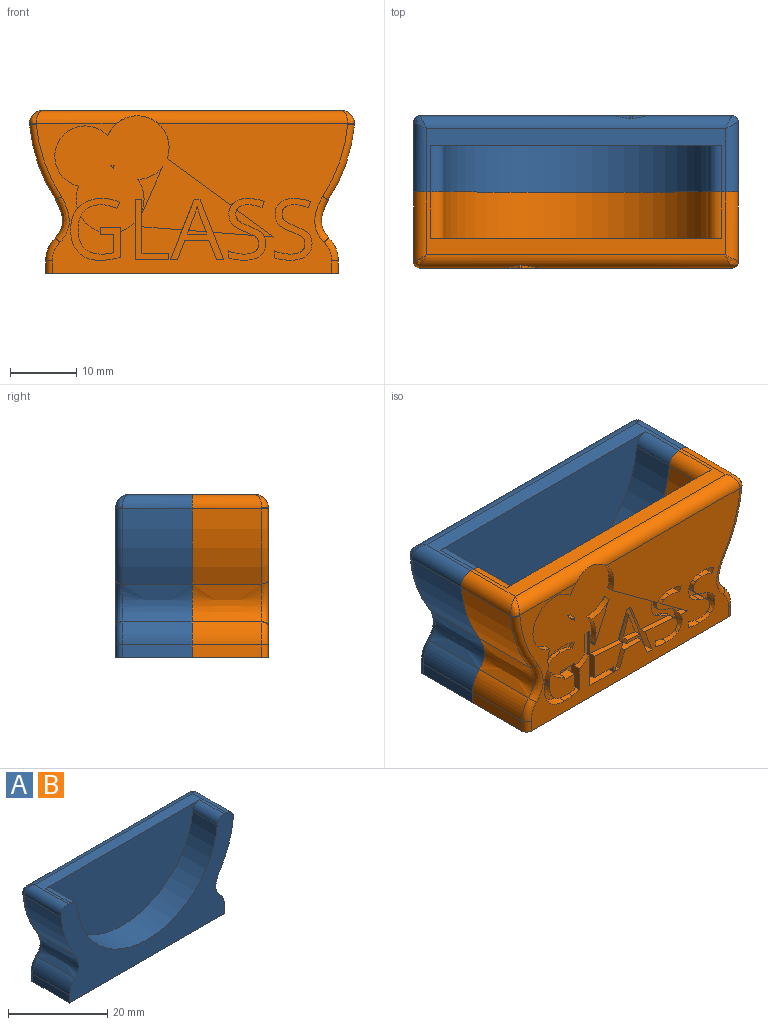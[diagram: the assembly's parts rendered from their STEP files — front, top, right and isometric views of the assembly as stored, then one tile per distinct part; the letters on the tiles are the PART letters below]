
ASSEMBLY  parts=2 mates=1
PART A: 149 faces, bbox 53x11.5x24.6 mm
  f0: plane 46.98x22.58mm, normal (0,1,0), area 539.3mm2, adj f3,f5,f8,f9,f10,f11,f12,f22
  f1: plane 5.75x5.37mm, normal (0,1,0), area 18.2mm2, adj f4,f84,f85,f88,f89,f90,f91,f92
  f2: plane 7.04x3.75mm, normal (0,1,0), area 6.8mm2, adj f6,f7,f27,f77
  f3: cylinder r=5.13mm len=2.17mm, axis (0,1,0), area 2.6mm2, adj f0,f13,f76,f83
  f4: cylinder r=5.13mm len=2.94mm, axis (0,1,0), area 3.8mm2, adj f1,f13,f84,f85
  f5: cylinder r=5.13mm len=3.39mm, axis (0,1,0), area 3.5mm2, adj f0,f13,f26,f86
  f6: cylinder r=5.13mm len=4.74mm, axis (0,1,0), area 5mm2, adj f2,f13,f27,f77
  f7: plane 7.04x3.12mm, normal (-0.91,0,-0.4), area 7.7mm2, adj f2,f13,f27,f77
  f8: plane 6.04x1mm, normal (-0.08,0,1), area 6.1mm2, adj f0,f13,f59,f77
  f9: plane 6.11x1mm, normal (-0.08,0,1), area 6.1mm2, adj f0,f13,f33,f60
  f10: plane 1.44x1mm, normal (-0.08,0,1), area 1.4mm2, adj f0,f11,f14,f34
  f11: plane 5.59x4.1mm, normal (0.59,0,-0.81), area 6.9mm2, adj f0,f10,f14,f35
  f12: plane 9.65x7.08mm, normal (0.59,0,-0.81), area 12mm2, adj f0,f13,f31,f36
  f13: plane 29.97x18.05mm, normal (0,1,0), area 275.3mm2, adj f3,f4,f5,f6,f7,f8,f9,f12
  f14: plane 5.72x4.11mm, normal (0,1,0), area 5.1mm2, adj f10,f11,f34,f35,f46,f47,f48,f49
  f15: extruded ~10.5x5.69mm, area 65mm2, adj f16,f24,f141,f145
  f16: cylinder r=24.58mm len=11.32mm, axis (0,1,0), area 127.1mm2, adj f15,f24,f131,f142
  f17: cylinder r=20mm len=39.83mm, axis (0,1,0), area 414.3mm2, adj f24,f25,f133,f134
  f18: plane 44.98x9.5mm, normal (0,0,1), area 120.6mm2, adj f24,f25,f130,f131,f132,f133,f134
  f19: cylinder r=24.58mm len=11.32mm, axis (0,1,0), area 127.1mm2, adj f20,f24,f130,f137
  f20: extruded ~10.5x5.69mm, area 65mm2, adj f19,f24,f136,f147
  f21: plane 10.5x1.89mm, normal (-1,0,0), area 19.9mm2, adj f22,f24,f135,f147
  f22: plane 44.12x11.5mm, normal (0,0,-1), area 506.9mm2, adj f0,f21,f23,f24,f135,f140
  f23: plane 10.5x1.89mm, normal (1,0,0), area 19.9mm2, adj f22,f24,f140,f145
  f24: plane 48.98x24.58mm, normal (0,-1,0), area 457.7mm2, adj f15,f16,f17,f18,f19,f20,f21,f22
  f25: plane 43.82x20mm, normal (0,-1,0), area 629.8mm2, adj f17,f18,f133,f134
  f26: cylinder r=4.59mm len=9.07mm, axis (0,1,0), area 17.2mm2, adj f0,f5,f13,f31
  f27: cylinder r=4.8mm len=3.75mm, axis (0,1,0), area 4.3mm2, adj f2,f6,f7,f13
  f28: cylinder r=4.59mm len=1mm, axis (0,1,0), area 0.5mm2, adj f13,f29,f30,f32
  f29: cylinder r=4.8mm len=1mm, axis (0,1,0), area 0.6mm2, adj f13,f28,f30,f32
  f30: cylinder r=5.13mm len=1mm, axis (0,1,0), area 0.6mm2, adj f13,f28,f29,f32
  f31: cylinder r=4.8mm len=9.26mm, axis (0,1,0), area 15mm2, adj f0,f12,f13,f26,f132
  f32: plane 0.55x0.5mm, normal (0,1,0), area 0.1mm2, adj f28,f29,f30
  f33: extruded ~1.6x0.63mm, area 1.3mm2, adj f0,f9,f13,f37,f57,f58
  f34: extruded ~1.6x1.51mm, area 2.1mm2, adj f0,f10,f14,f45,f46,f58
  f35: extruded ~1.6x1mm, area 1.2mm2, adj f0,f11,f14,f49,f50,f58
  f36: extruded ~1.67x1.6mm, area 1.8mm2, adj f0,f12,f13,f54,f55,f58
  f37: extruded ~1.6x0.77mm, area 1.3mm2, adj f0,f33,f38,f58
  f38: extruded ~1.6x1.11mm, area 2.1mm2, adj f0,f37,f39,f58
  f39: extruded ~1.6x1.59mm, area 2.7mm2, adj f0,f38,f40,f58
  f40: extruded ~1.6x1.3mm, area 2.1mm2, adj f0,f39,f41,f58
  f41: extruded ~1.6x1.22mm, area 2mm2, adj f0,f40,f42,f58
  f42: plane 1.6x1.02mm, normal (-1,0,0), area 1.6mm2, adj f0,f41,f43,f58
  f43: extruded ~2.48x1.6mm, area 4.1mm2, adj f0,f42,f44,f58
  f44: extruded ~2.35x1.6mm, area 4mm2, adj f0,f43,f45,f58
  f45: extruded ~1.87x1.6mm, area 3.4mm2, adj f0,f34,f44,f58
  f46: extruded ~1.96x1.09mm, area 1.4mm2, adj f14,f34,f47,f58
  f47: extruded ~1.26x0.6mm, area 0.8mm2, adj f14,f46,f48,f58
  f48: extruded ~0.6x0.59mm, area 0.5mm2, adj f14,f47,f49,f58
  f49: extruded ~0.77x0.6mm, area 0.5mm2, adj f14,f35,f48,f58
  f50: extruded ~1.6x1.31mm, area 2.2mm2, adj f0,f35,f51,f58
  f51: extruded ~2.18x1.6mm, area 3.6mm2, adj f0,f50,f52,f58
  f52: plane 1.6x0.92mm, normal (0.94,0,0.34), area 1.6mm2, adj f0,f51,f53,f58
  f53: extruded ~2.48x1.6mm, area 4.1mm2, adj f0,f52,f54,f58
  f54: extruded ~2.08x1.6mm, area 3.5mm2, adj f0,f36,f53,f58
  f55: extruded ~1.62x0.6mm, area 1mm2, adj f13,f36,f56,f58
  f56: extruded ~1.81x1.07mm, area 1.3mm2, adj f13,f55,f57,f58
  f57: extruded ~1.35x0.6mm, area 0.9mm2, adj f13,f33,f56,f58
  f58: plane 9.31x5.7mm, normal (0,1,0), area 19mm2, adj f33,f34,f35,f36,f37,f38,f39,f40
  f59: plane 9.1x3.58mm, normal (-0.93,0,-0.37), area 10.7mm2, adj f0,f8,f13,f63,f71,f72
  f60: plane 9.1x3.56mm, normal (0.93,0,-0.36), area 10.3mm2, adj f0,f9,f13,f67,f71,f72
  f61: plane 2.81x1.6mm, normal (0.94,0,0.35), area 2.4mm2, adj f68,f70,f72,f73,f74,f75
  f62: plane 2.81x1.6mm, normal (-0.94,0,0.35), area 2.2mm2, adj f69,f70,f72,f73,f74,f75
  f63: plane 1.6x1.07mm, normal (0,0,1), area 1.7mm2, adj f0,f59,f64,f72
  f64: plane 2.88x1.6mm, normal (0.93,0,0.36), area 4.9mm2, adj f0,f63,f65,f72
  f65: plane 3.63x1.6mm, normal (0,0,1), area 5.8mm2, adj f0,f64,f66,f72
  f66: plane 2.88x1.6mm, normal (-0.93,0,0.36), area 5mm2, adj f0,f65,f67,f72
  f67: plane 1.6x1.09mm, normal (0,0,1), area 1.7mm2, adj f0,f60,f66,f72
  f68: extruded ~1.31x0.6mm, area 0.8mm2, adj f61,f69,f72,f73
  f69: extruded ~1.31x0.6mm, area 0.8mm2, adj f62,f68,f72,f73
  f70: plane 2.93x1.6mm, normal (0,0,-1), area 4.7mm2, adj f61,f62,f72,f75
  f71: plane 0.89x0.6mm, normal (0,0,-1), area 0.5mm2, adj f13,f59,f60,f72
  f72: plane 9.1x8.03mm, normal (0,1,0), area 21.1mm2, adj f59,f60,f61,f62,f63,f64,f65,f66
  f73: plane 3.77x2.59mm, normal (0,1,0), area 4.5mm2, adj f61,f62,f68,f69,f74
  f74: plane 2.59x1mm, normal (-0.08,0,1), area 2.6mm2, adj f61,f62,f73,f75
  f75: plane 2.93x0.55mm, normal (0,1,0), area 1.2mm2, adj f61,f62,f70,f74
  f76: plane 9.06x1.6mm, normal (-1,0,0), area 11mm2, adj f0,f3,f13,f78,f81,f82
  f77: plane 8.11x1.6mm, normal (1,0,0), area 9.2mm2, adj f0,f2,f6,f7,f8,f13,f80,f81
  f78: plane 5.05x1.6mm, normal (0,0,1), area 8.1mm2, adj f0,f76,f79,f82
  f79: plane 1.6x0.95mm, normal (1,0,0), area 1.5mm2, adj f0,f78,f80,f82
  f80: plane 4x1.6mm, normal (0,0,-1), area 6.4mm2, adj f0,f77,f79,f82
  f81: plane 1.05x0.6mm, normal (0,0,-1), area 0.6mm2, adj f13,f76,f77,f82
  f82: plane 9.06x5.05mm, normal (0,1,0), area 13.4mm2, adj f76,f77,f78,f79,f80,f81
  f83: plane 4.41x1.6mm, normal (1,0,0), area 6.5mm2, adj f0,f3,f13,f87,f102,f103
  f84: plane 1.6x0.94mm, normal (-1,0,0), area 0.9mm2, adj f1,f4,f13,f87,f88,f103
  f85: extruded ~2.73x1.6mm, area 3.8mm2, adj f1,f4,f13,f92,f93,f103
  f86: extruded ~1.63x1.62mm, area 2.2mm2, adj f0,f5,f13,f97,f98,f103
  f87: plane 3.08x0.6mm, normal (0,0,-1), area 1.8mm2, adj f13,f83,f84,f103
  f88: plane 2.02x1.6mm, normal (0,0,1), area 3.2mm2, adj f1,f84,f89,f103
  f89: plane 2.79x1.6mm, normal (-1,0,0), area 4.5mm2, adj f1,f88,f90,f103
  f90: extruded ~1.84x1.6mm, area 3mm2, adj f1,f89,f91,f103
  f91: extruded ~2.63x1.6mm, area 4.6mm2, adj f1,f90,f92,f103
  f92: extruded ~2.78x1.6mm, area 4.8mm2, adj f1,f85,f91,f103
  f93: extruded ~2.58x0.98mm, area 1.7mm2, adj f13,f85,f94,f103
  f94: extruded ~2.36x0.6mm, area 1.5mm2, adj f13,f93,f95,f103
  f95: plane 0.93x0.6mm, normal (0.92,0,0.4), area 0.6mm2, adj f13,f94,f96,f103
  f96: extruded ~2.7x0.6mm, area 1.7mm2, adj f13,f95,f97,f103
  f97: extruded ~2.5x0.6mm, area 1.5mm2, adj f13,f86,f96,f103
  f98: extruded ~2.48x1.6mm, area 4.1mm2, adj f0,f86,f99,f103
  f99: extruded ~3.43x1.6mm, area 5.9mm2, adj f0,f98,f100,f103
  f100: extruded ~3.2x1.6mm, area 5.6mm2, adj f0,f99,f101,f103
  f101: extruded ~1.72x1.6mm, area 2.8mm2, adj f0,f100,f102,f103
  f102: extruded ~1.6x1.46mm, area 2.4mm2, adj f0,f83,f101,f103
  f103: plane 9.31x7.53mm, normal (0,1,0), area 24.8mm2, adj f83,f84,f85,f86,f87,f88,f89,f90
  f104: extruded ~1.87x1.6mm, area 3.4mm2, adj f0,f105,f128,f129
  f105: extruded ~1.6x1.51mm, area 2.6mm2, adj f0,f104,f106,f129
  f106: extruded ~1.96x1.6mm, area 3.6mm2, adj f0,f105,f107,f129
  f107: extruded ~1.6x1.26mm, area 2.2mm2, adj f0,f106,f108,f129
  f108: extruded ~1.6x0.59mm, area 1.3mm2, adj f0,f107,f109,f129
  f109: extruded ~1.6x0.77mm, area 1.3mm2, adj f0,f108,f110,f129
  f110: extruded ~1.6x1mm, area 1.8mm2, adj f0,f109,f111,f129
  f111: extruded ~1.6x1.31mm, area 2.2mm2, adj f0,f110,f112,f129
  f112: extruded ~2.18x1.6mm, area 3.6mm2, adj f0,f111,f113,f129
  f113: plane 1.6x0.92mm, normal (0.94,0,0.34), area 1.6mm2, adj f0,f112,f114,f129
  f114: extruded ~2.48x1.6mm, area 4.1mm2, adj f0,f113,f115,f129
  f115: extruded ~2.08x1.6mm, area 3.5mm2, adj f0,f114,f116,f129
  f116: extruded ~1.67x1.6mm, area 3.1mm2, adj f0,f115,f117,f129
  f117: extruded ~1.62x1.6mm, area 2.8mm2, adj f0,f116,f118,f129
  f118: extruded ~1.81x1.6mm, area 3.4mm2, adj f0,f117,f119,f129
  f119: extruded ~1.6x1.35mm, area 2.3mm2, adj f0,f118,f120,f129
  f120: extruded ~1.6x0.63mm, area 1.4mm2, adj f0,f119,f121,f129
  f121: extruded ~1.6x0.77mm, area 1.3mm2, adj f0,f120,f122,f129
  f122: extruded ~1.6x1.11mm, area 2.1mm2, adj f0,f121,f123,f129
  f123: extruded ~1.6x1.59mm, area 2.7mm2, adj f0,f122,f124,f129
  f124: extruded ~1.6x1.3mm, area 2.1mm2, adj f0,f123,f125,f129
  f125: extruded ~1.6x1.22mm, area 2mm2, adj f0,f124,f126,f129
  f126: plane 1.6x1.02mm, normal (-1,0,0), area 1.6mm2, adj f0,f125,f127,f129
  f127: extruded ~2.48x1.6mm, area 4.1mm2, adj f0,f126,f128,f129
  f128: extruded ~2.35x1.6mm, area 4mm2, adj f0,f104,f127,f129
  f129: plane 9.31x5.7mm, normal (0,1,0), area 19mm2, adj f104,f105,f106,f107,f108,f109,f110,f111
  f130: cylinder r=2mm len=10.5mm, axis (0,1,0), area 33.7mm2, adj f18,f19,f24,f138,f139
  f131: cylinder r=2mm len=10.5mm, axis (0,1,0), area 33.7mm2, adj f16,f18,f24,f143,f144
  f132: cylinder r=2mm len=46.98mm, axis (-1,0,0), area 138.9mm2, adj f0,f18,f31,f139,f144
  f133: cylinder r=2mm len=7mm, axis (0,1,0), area 20.7mm2, adj f17,f18,f24,f25
  f134: cylinder r=2mm len=7mm, axis (0,1,0), area 20.7mm2, adj f17,f18,f24,f25
  f135: cylinder r=1mm len=1.89mm, axis (0,0,-1), area 3mm2, adj f0,f21,f22,f148
  f136: bspline ~8.59x2.74mm, area 10.5mm2, adj f0,f20,f137,f148
  f137: torus R=23.58mm, axis (0,-1,0), area 18.8mm2, adj f0,f19,f136,f138
  f138: torus R=1mm, axis (0,-1,0), area 0.2mm2, adj f0,f130,f137,f139
  f139: bspline ~2.39x2mm, area 2.2mm2, adj f130,f132,f138
  f140: cylinder r=1mm len=1.89mm, axis (0,0,1), area 3mm2, adj f0,f22,f23,f146
  f141: bspline ~8.72x2.87mm, area 10.5mm2, adj f0,f15,f142,f146
  f142: torus R=23.58mm, axis (0,-1,0), area 18.8mm2, adj f0,f16,f141,f143
  f143: torus R=1mm, axis (0,-1,0), area 0.2mm2, adj f0,f131,f142,f144
  f144: bspline ~2.1x2mm, area 2.2mm2, adj f131,f132,f143
  f145: cylinder r=5mm len=10.5mm, axis (0,1,0), area 40.7mm2, adj f15,f23,f24,f146
  f146: torus R=4mm, axis (0,-1,0), area 5.7mm2, adj f0,f140,f141,f145
  f147: cylinder r=5mm len=10.5mm, axis (0,1,0), area 40.7mm2, adj f20,f21,f24,f148
  f148: torus R=4mm, axis (0,-1,0), area 5.7mm2, adj f0,f135,f136,f147
PART B: same geometry as A
PLACE A rot(axis=(0,0,1),0deg) t=(-45.21,-33.27,-18.35)mm
PLACE B rot(axis=(0,0,-1),180deg) t=(-45.21,-47.27,-18.35)mm
MATE fastened A.f24 <-> B.f24  axis (0,-1,0) through (-45.21,-40.27,-42.93)mm
